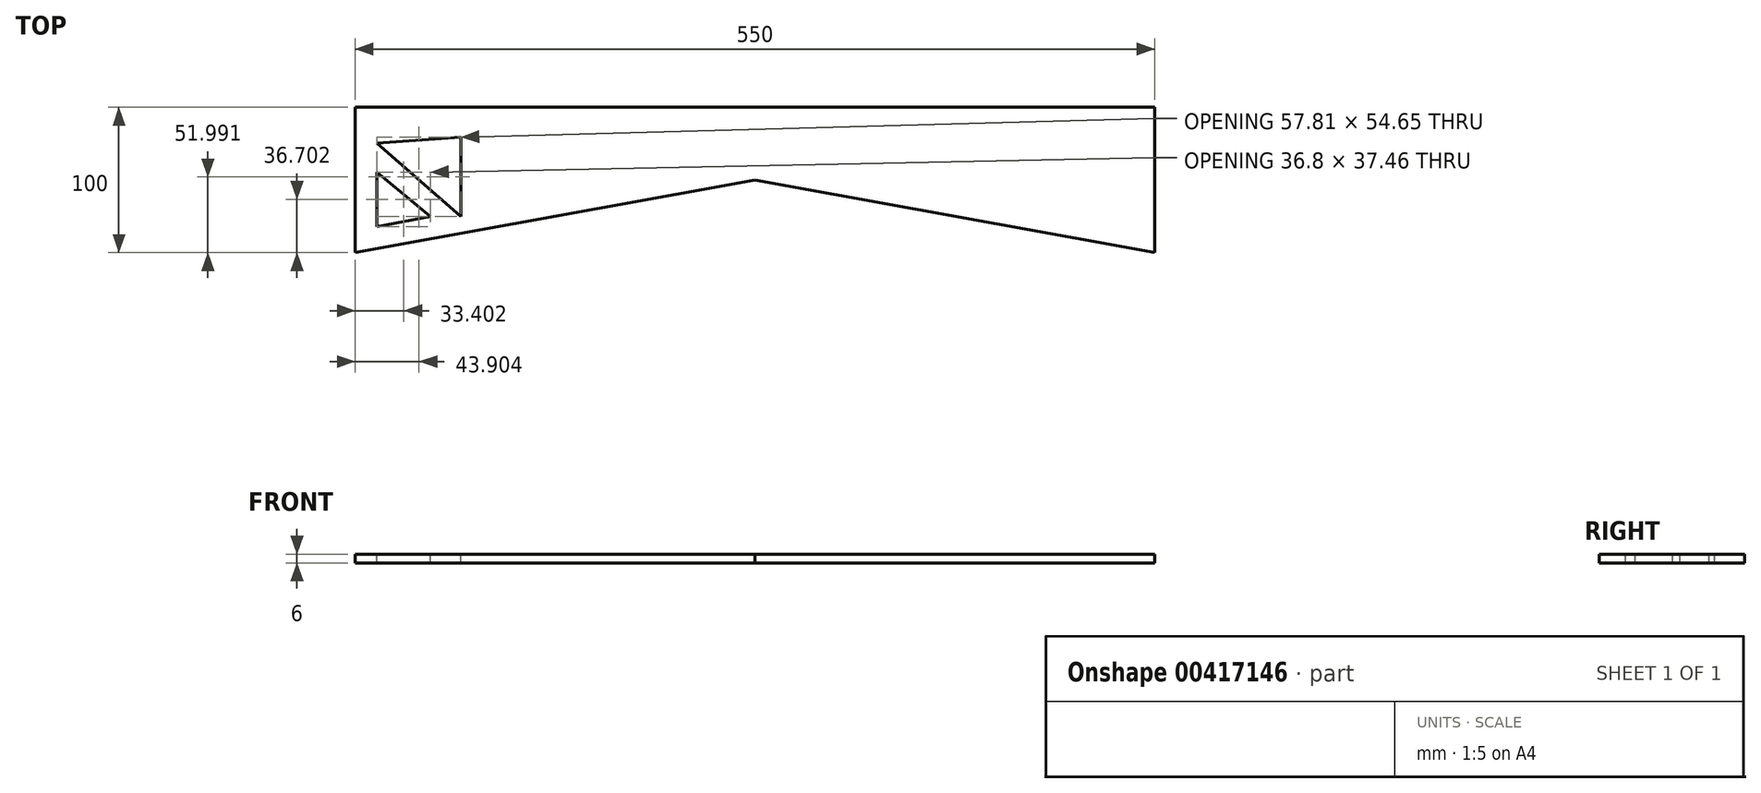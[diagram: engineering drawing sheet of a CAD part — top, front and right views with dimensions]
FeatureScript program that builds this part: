
annotation { "Feature Type Name" : "Feature", "Feature Type Description" : "" }
export const myFeature = defineFeature(function(context is Context, id is Id, definition is map)
    precondition{}
    {
        {
            var Q0;
            Q0=qCreatedBy(makeId("Top.planeOp"),FACE);
            var sketch = newSketch(context, id + "F0", { "sketchPlane" : qUnion([Q0])});
            skLineSegment(sketch, "E0.bottom", {"start": v(275, 50) * mm, "end": v(-275, 50) * mm});
            skLineSegment(sketch, "E0.top", {"start": v(275, -50) * mm, "end": v(-275, -50) * mm});
            skLineSegment(sketch, "E0.left", {"start": v(275, 50) * mm, "end": v(275, -50) * mm});
            skLineSegment(sketch, "E0.right", {"start": v(-275, 50) * mm, "end": v(-275, -50) * mm});
            skPoint(sketch, "E0.middle", {"position": v(0, 0) * mm});
            skLineSegment(sketch, "E1", {"start": v(0, 0) * mm, "end": v(-275, -50) * mm});
            skLineSegment(sketch, "E2", {"start": v(0, 0) * mm, "end": v(275, -50) * mm});
            skSolve(sketch);
        }
        {
            var Q0;
            Q0=makeQuery(id+"F0.imprint","IMPRINT",FACE,{"disambiguationData":[TD([[makeQuery(id+"F0.imprint","IMPRINT",EDGE,{"derivedFrom":sQuery(id+"F0.wireOp",EDGE,"E0.bottom")}),1.0]])]});
            extrude(context, id + "F1", {"entities" : qUnion([Q0]), "depth" : 6 * mm});
        }
        {
            var Q0;
            Q0=makeQuery(id+"F1.opExtrude","CAP_FACE",FACE,{"disambiguationData":[OSD([sQuery(id+"F0.wireOp",EDGE,"E0.bottom"),sQuery(id+"F0.wireOp",EDGE,"E0.left"),sQuery(id+"F0.wireOp",EDGE,"E0.right"),sQuery(id+"F0.wireOp",EDGE,"E1"),sQuery(id+"F0.wireOp",EDGE,"E2")])],"isStart":false});
            var sketch = newSketch(context, id + "F2", { "sketchPlane" : qUnion([Q0])});
            skLineSegment(sketch, "E3", {"start": v(-260, 5.43) * mm, "end": v(-260, -32.03) * mm});
            skLineSegment(sketch, "E4", {"start": v(-260, -32.03) * mm, "end": v(-223.2, -25.34) * mm});
            skLineSegment(sketch, "E5", {"start": v(-260, 5.43) * mm, "end": v(-223.2, -25.34) * mm});
            skLineSegment(sketch, "E6", {"start": v(-260, 25.45) * mm, "end": v(-202.2, -25.34) * mm});
            skLineSegment(sketch, "E7", {"start": v(-202.2, -25.34) * mm, "end": v(-202.2, 29.32) * mm});
            skLineSegment(sketch, "E8", {"start": v(-202.2, 29.32) * mm, "end": v(-260, 25.45) * mm});
            skSolve(sketch);
        }
        {
            var Q0;
            Q0=makeQuery(id+"F2.imprint","IMPRINT",FACE,{"disambiguationData":[TD([[makeQuery(id+"F2.imprint","IMPRINT",EDGE,{"derivedFrom":sQuery(id+"F2.wireOp",EDGE,"E3")}),1.0]])]});
            var Q1;
            Q1=makeQuery(id+"F2.imprint","IMPRINT",FACE,{"disambiguationData":[TD([[makeQuery(id+"F2.imprint","IMPRINT",EDGE,{"derivedFrom":sQuery(id+"F2.wireOp",EDGE,"E6")}),1.0]])]});
            extrude(context, id + "F3", {"entities" : qUnion([Q0, Q1]), "operationType" : NewBodyOperationType.REMOVE, "oppositeDirection" : true, "depth" : 25 * mm});
        }
    });
